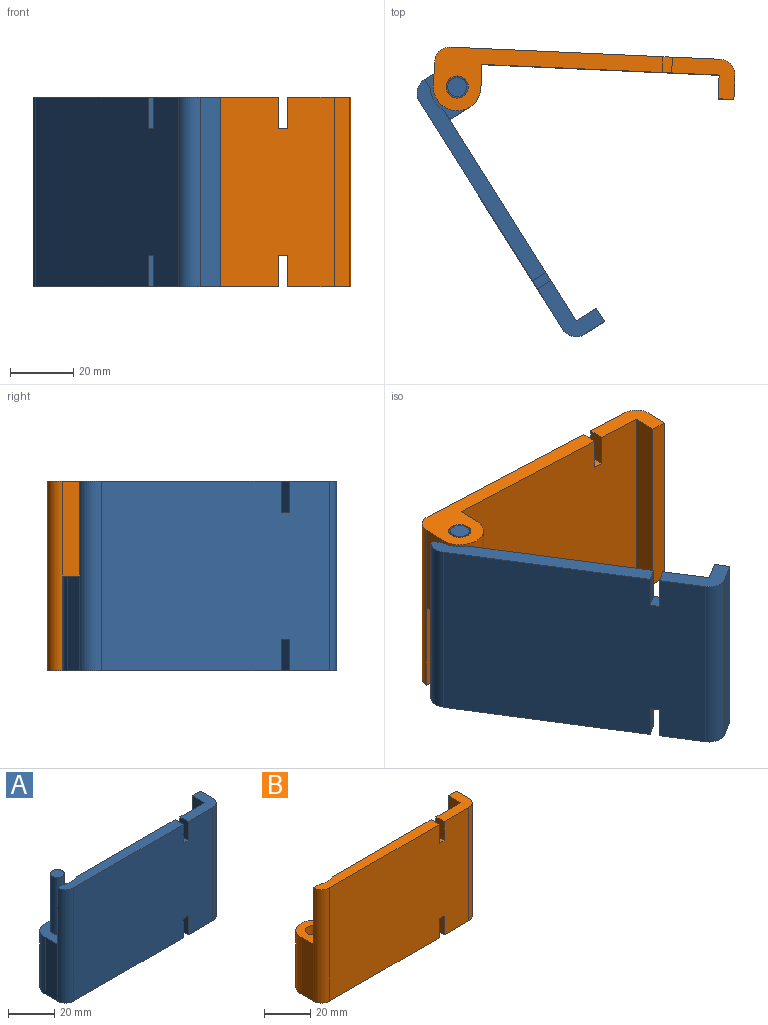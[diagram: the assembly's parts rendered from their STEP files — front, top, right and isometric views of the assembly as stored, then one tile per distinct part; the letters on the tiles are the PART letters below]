
ASSEMBLY  parts=2 mates=1
PART A: 25 faces, bbox 95x20x60 mm
  f0: plane 78.5x60mm, normal (0,1,0), area 4545mm2, adj f2,f3,f4,f5,f10,f11,f12,f14
  f1: plane 85x60mm, normal (0,-1,0), area 5040mm2, adj f2,f3,f10,f11,f17,f18,f19,f20
  f2: plane 20x12.5mm, normal (0,0,1), area 132.1mm2, adj f0,f1,f4,f8,f9,f17,f24
  f3: plane 20x12.5mm, normal (0,0,-1), area 132.1mm2, adj f0,f1,f4,f8,f9,f20,f24
  f4: plane 60x7.5mm, normal (-1,0,0), area 450mm2, adj f0,f2,f3,f9
  f5: cylinder r=8.5mm len=30mm, axis (0,0,-1), area 249.9mm2, adj f0,f6,f10,f14
  f6: plane 30x3.5mm, normal (0,1,0), area 105mm2, adj f5,f10,f14,f23
  f7: plane 30x7.5mm, normal (-1,0,0), area 225mm2, adj f11,f13,f14,f23
  f8: plane 60x7.5mm, normal (1,0,0), area 450mm2, adj f2,f3,f9,f24
  f9: plane 60x5mm, normal (0,1,0), area 300mm2, adj f2,f3,f4,f8
  f10: plane 72x5mm, normal (0,0,1), area 349.2mm2, adj f0,f1,f5,f6,f18,f23
  f11: plane 72x20mm, normal (0,0,-1), area 555.5mm2, adj f0,f1,f7,f12,f13,f22,f23
  f12: plane 30x7.5mm, normal (1,0,0), area 225mm2, adj f0,f11,f13,f14
  f13: cylinder r=7.5mm len=30mm, axis (0,0,-1), area 706.9mm2, adj f7,f11,f12,f14
  f14: plane 16x15mm, normal (0,0,1), area 178mm2, adj f0,f5,f6,f7,f12,f13,f16
  f15: plane 6x6mm, normal (0,0,1), area 28.3mm2, adj f16
  f16: cylinder r=3mm len=30mm, axis (0,0,-1), area 565.5mm2, adj f14,f15
  f17: plane 10x5mm, normal (-1,0,0), area 50mm2, adj f0,f1,f2,f19
  f18: plane 10x5mm, normal (1,0,0), area 50mm2, adj f0,f1,f10,f19
  f19: plane 5x3mm, normal (0,0,1), area 15mm2, adj f0,f1,f17,f18
  f20: plane 10x5mm, normal (-1,0,0), area 50mm2, adj f0,f1,f3,f21
  f21: plane 5x3mm, normal (0,0,-1), area 15mm2, adj f0,f1,f20,f22
  f22: plane 10x5mm, normal (1,0,0), area 50mm2, adj f0,f1,f11,f21
  f23: cylinder r=5mm len=60mm, axis (0,0,-1), area 471.2mm2, adj f1,f6,f7,f10,f11
  f24: cylinder r=5mm len=60mm, axis (0,0,1), area 471.2mm2, adj f1,f2,f3,f8
PART B: 24 faces, bbox 95x20x60 mm
  f0: plane 78.5x60mm, normal (0,1,0), area 4545mm2, adj f2,f3,f4,f5,f10,f11,f12,f15
  f1: plane 85x60mm, normal (0,-1,0), area 5040mm2, adj f2,f3,f10,f11,f16,f17,f18,f19
  f2: plane 20x12.5mm, normal (0,0,1), area 132.1mm2, adj f0,f1,f4,f8,f9,f16,f23
  f3: plane 20x12.5mm, normal (0,0,-1), area 132.1mm2, adj f0,f1,f4,f8,f9,f19,f23
  f4: plane 60x7.5mm, normal (-1,0,0), area 450mm2, adj f0,f2,f3,f9
  f5: cylinder r=8.5mm len=30mm, axis (0,0,-1), area 249.9mm2, adj f0,f6,f10,f15
  f6: plane 30x3.5mm, normal (0,1,0), area 105mm2, adj f5,f10,f15,f22
  f7: plane 30x7.5mm, normal (-1,0,0), area 225mm2, adj f11,f13,f15,f22
  f8: plane 60x7.5mm, normal (1,0,0), area 450mm2, adj f2,f3,f9,f23
  f9: plane 60x5mm, normal (0,1,0), area 300mm2, adj f2,f3,f4,f8
  f10: plane 72x5mm, normal (0,0,1), area 349.2mm2, adj f0,f1,f5,f6,f17,f22
  f11: plane 72x20mm, normal (0,0,-1), area 517mm2, adj f0,f1,f7,f12,f13,f14,f21,f22
  f12: plane 30x7.5mm, normal (1,0,0), area 225mm2, adj f0,f11,f13,f15
  f13: cylinder r=7.5mm len=30mm, axis (0,0,-1), area 706.9mm2, adj f7,f11,f12,f15
  f14: cylinder r=3.5mm len=30mm, axis (0,0,-1), area 659.7mm2, adj f11,f15
  f15: plane 16x15mm, normal (0,0,1), area 167.8mm2, adj f0,f5,f6,f7,f12,f13,f14
  f16: plane 10x5mm, normal (-1,0,0), area 50mm2, adj f0,f1,f2,f18
  f17: plane 10x5mm, normal (1,0,0), area 50mm2, adj f0,f1,f10,f18
  f18: plane 5x3mm, normal (0,0,1), area 15mm2, adj f0,f1,f16,f17
  f19: plane 10x5mm, normal (-1,0,0), area 50mm2, adj f0,f1,f3,f20
  f20: plane 5x3mm, normal (0,0,-1), area 15mm2, adj f0,f1,f19,f21
  f21: plane 10x5mm, normal (1,0,0), area 50mm2, adj f0,f1,f11,f20
  f22: cylinder r=5mm len=60mm, axis (0,0,-1), area 471.2mm2, adj f1,f6,f7,f10,f11
  f23: cylinder r=5mm len=60mm, axis (0,0,1), area 471.2mm2, adj f1,f2,f3,f8
PLACE A rot(axis=(0,0,-1),57.8deg) t=(8.63,48.91,-9.59)mm
PLACE B rot(axis=(1,-0.02,0),180deg) t=(16.28,62.05,50.41)mm
MATE revolute A.f5 <-> B.f5  axis (0,0,1) through (23.21,49.22,50.41)mm
